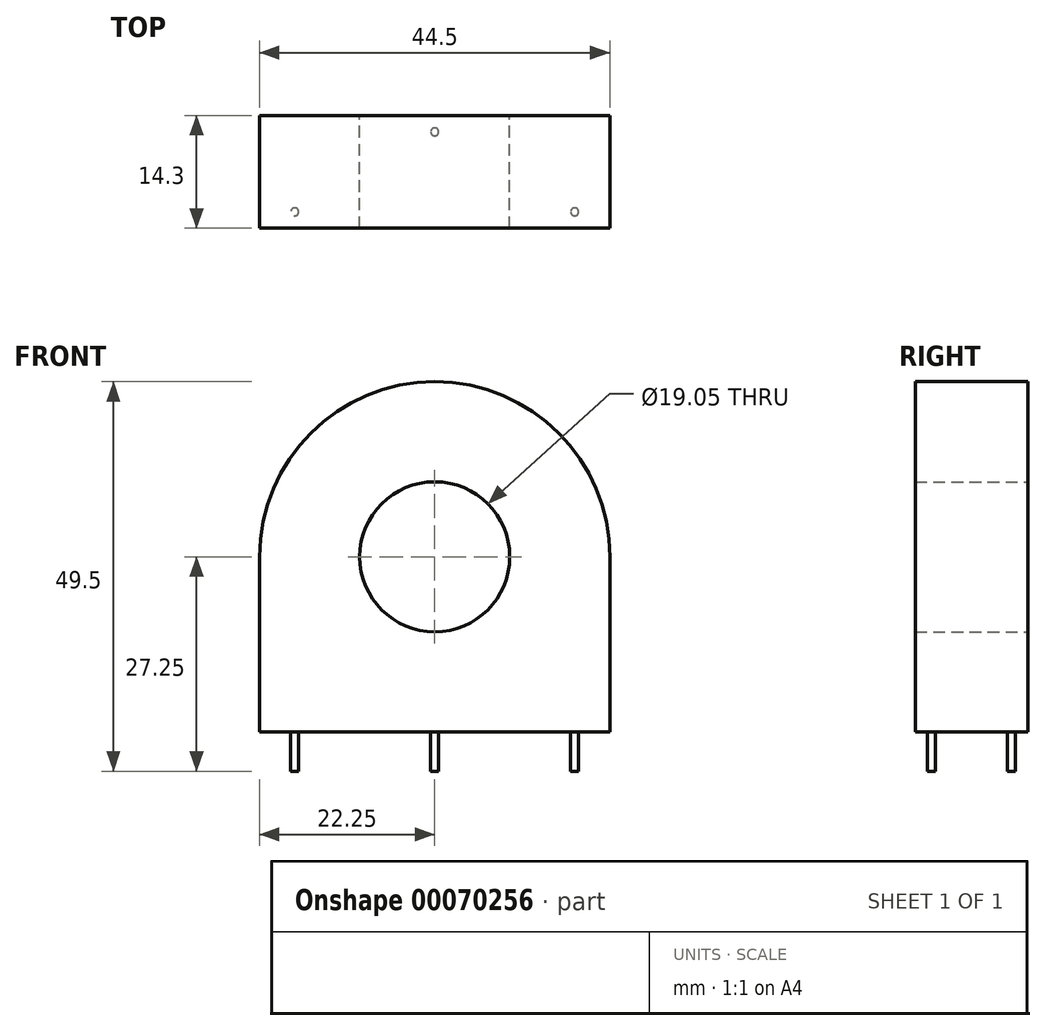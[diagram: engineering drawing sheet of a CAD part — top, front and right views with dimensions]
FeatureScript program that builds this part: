
annotation { "Feature Type Name" : "Feature", "Feature Type Description" : "" }
export const myFeature = defineFeature(function(context is Context, id is Id, definition is map)
    precondition{}
    {
        {
            var Q0;
            Q0=qCreatedBy(makeId("Front.planeOp"),FACE);
            var sketch = newSketch(context, id + "F0", { "sketchPlane" : qUnion([Q0])});
            skCircle(sketch, "E0", {"center": v(0, 22.25) * mm, "radius": 9.53 * mm});
            skLineSegment(sketch, "E1", {"start": v(-22.25, 22.25) * mm, "end": v(-22.25, 0) * mm});
            skLineSegment(sketch, "E2", {"start": v(-22.25, 0) * mm, "end": v(22.25, 0) * mm});
            skLineSegment(sketch, "E3", {"start": v(22.25, 0) * mm, "end": v(22.25, 22.25) * mm});
            skArc(sketch, "E4", {"start": v(-22.25, 22.25) * mm, "mid": v(0, 44.5) * mm, "end": v(22.25, 22.25) * mm});
            skSolve(sketch);
        }
        {
            var Q0;
            Q0 = qSketchRegion(id + "F0", true);
            extrude(context, id + "F1", {"entities" : qUnion([Q0]), "endBound" : BoundingType.SYMMETRIC, "depth" : 14.3 * mm});
        }
        {
            var Q0;
            Q0=makeQuery(id+"F1.opExtrude","SWEPT_FACE",FACE,{"disambiguationData":[OSD([sQuery(id+"F0.wireOp",EDGE,"E2")])]});
            var sketch = newSketch(context, id + "F2", { "sketchPlane" : qUnion([Q0])});
            skCircle(sketch, "E5", {"center": v(-17.78, 5.08) * mm, "radius": 0.5 * mm});
            skCircle(sketch, "E6.MirrorC", {"center": v(17.78, 5.08) * mm, "radius": 0.5 * mm});
            skCircle(sketch, "E7", {"center": v(0, -5.08) * mm, "radius": 0.5 * mm});
            skSolve(sketch);
        }
        {
            var Q0;
            Q0 = qSketchRegion(id + "F2", true);
            extrude(context, id + "F3", {"entities" : qUnion([Q0]), "operationType" : NewBodyOperationType.ADD, "depth" : 5 * mm});
        }
    });
